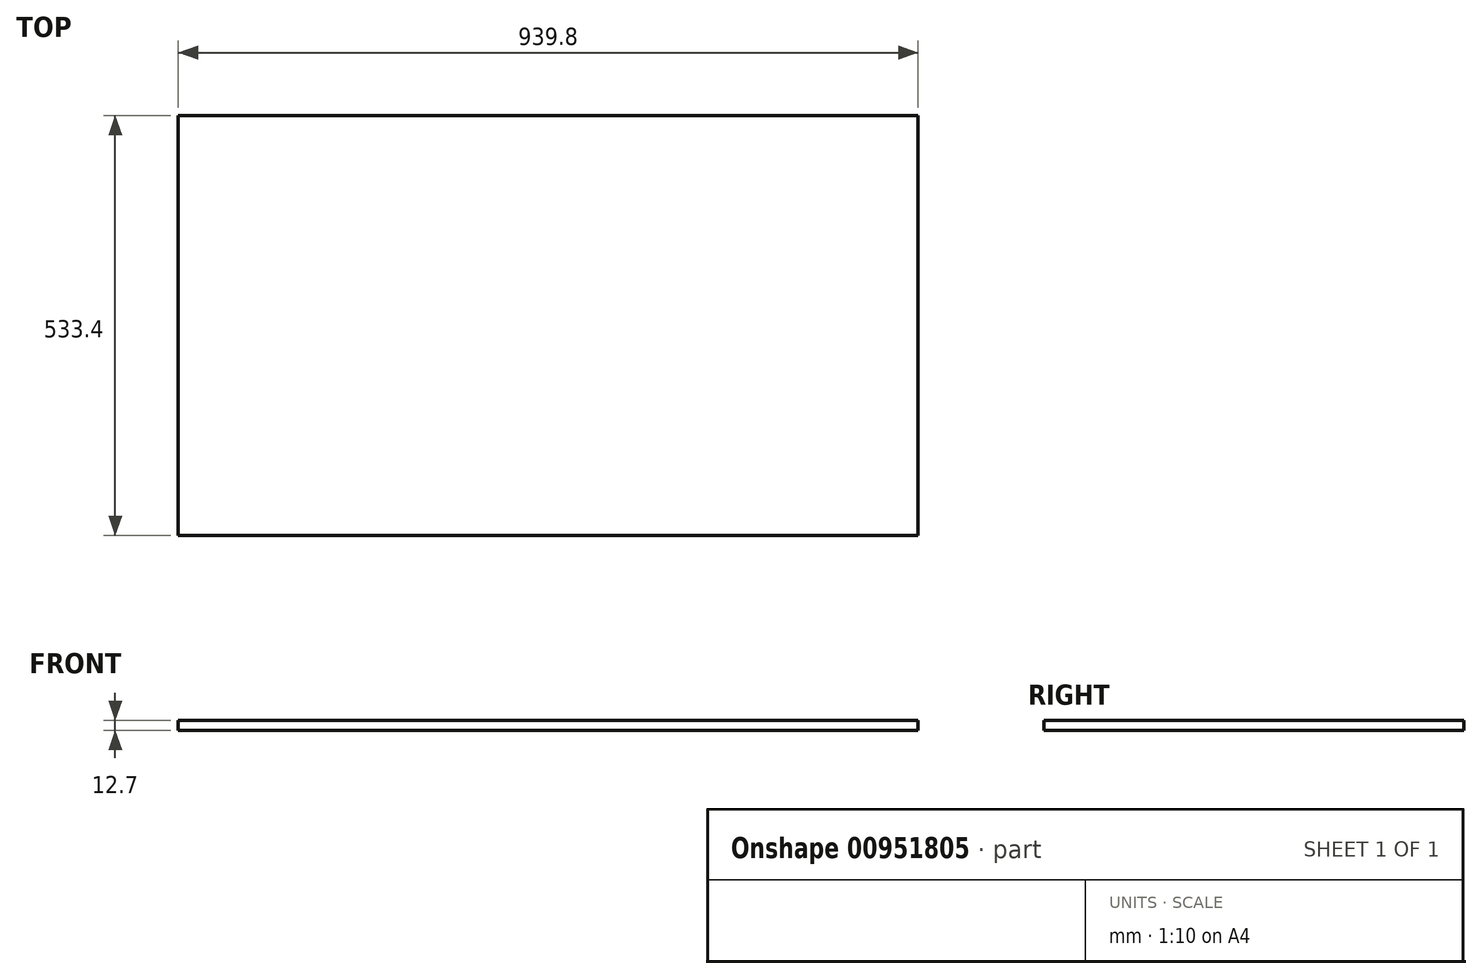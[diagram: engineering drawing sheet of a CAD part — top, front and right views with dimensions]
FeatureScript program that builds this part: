
annotation { "Feature Type Name" : "Feature", "Feature Type Description" : "" }
export const myFeature = defineFeature(function(context is Context, id is Id, definition is map)
    precondition{}
    {
        {
            var Q0;
            Q0=qCreatedBy(makeId("Top.planeOp"),FACE);
            var sketch = newSketch(context, id + "F0", { "sketchPlane" : qUnion([Q0])});
            skLineSegment(sketch, "E0.bottom", {"start": v(469.9, -266.7) * mm, "end": v(-469.9, -266.7) * mm});
            skLineSegment(sketch, "E0.top", {"start": v(469.9, 266.7) * mm, "end": v(-469.9, 266.7) * mm});
            skLineSegment(sketch, "E0.left", {"start": v(469.9, -266.7) * mm, "end": v(469.9, 266.7) * mm});
            skLineSegment(sketch, "E0.right", {"start": v(-469.9, -266.7) * mm, "end": v(-469.9, 266.7) * mm});
            skPoint(sketch, "E0.middle", {"position": v(0, 0) * mm});
            skSolve(sketch);
        }
        {
            var Q0;
            Q0 = qSketchRegion(id + "F0", true);
            extrude(context, id + "F1", {"entities" : qUnion([Q0]), "depth" : 12.7 * mm, "offsetDistance" : 25.4 * mm});
        }
    });
